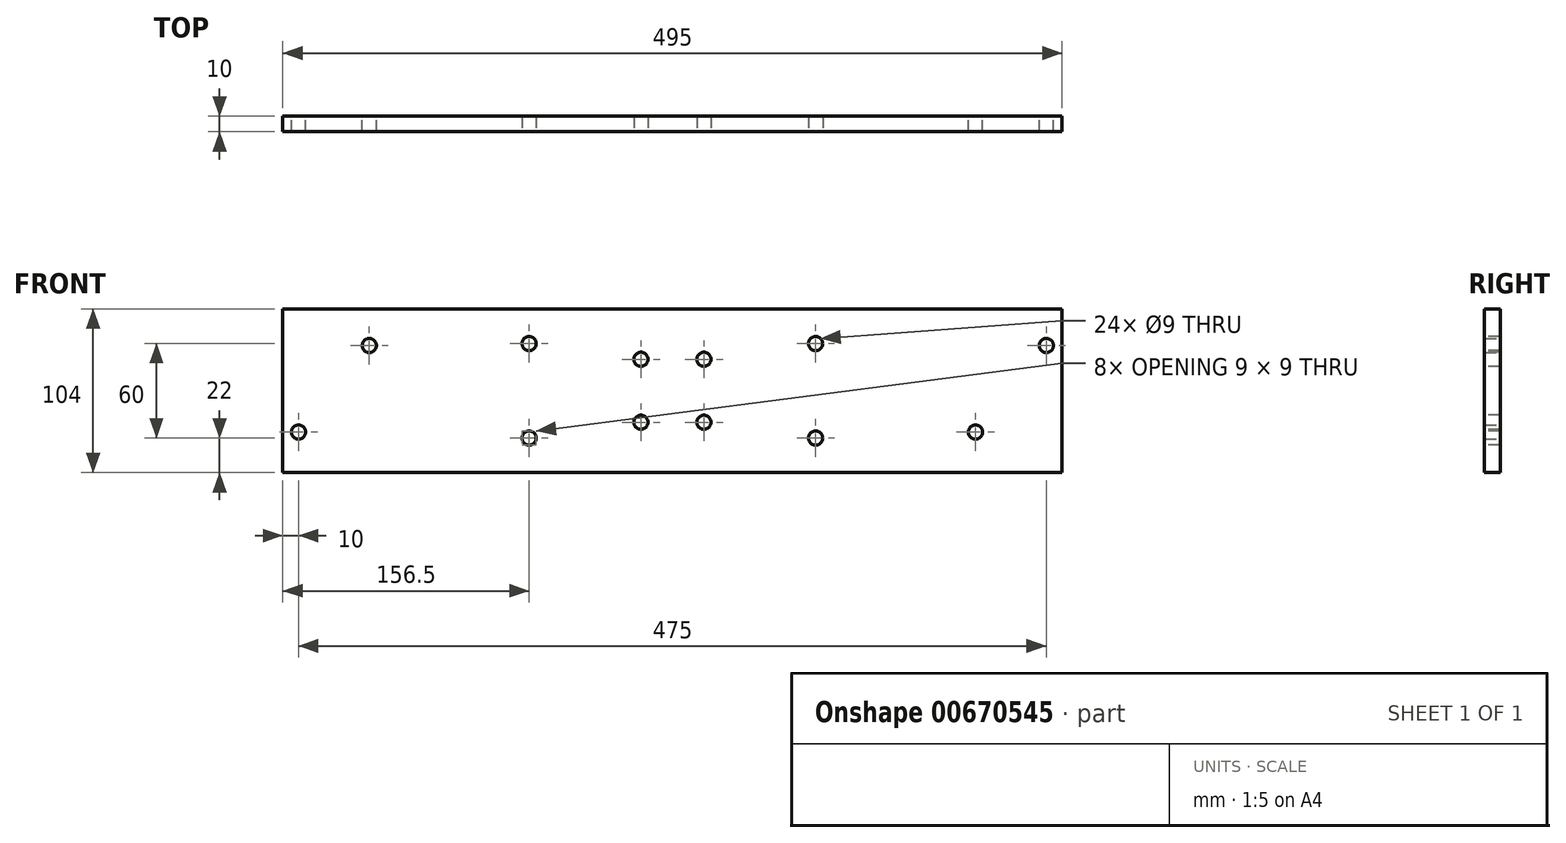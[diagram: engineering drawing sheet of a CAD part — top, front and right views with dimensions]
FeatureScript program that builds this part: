
annotation { "Feature Type Name" : "Feature", "Feature Type Description" : "" }
export const myFeature = defineFeature(function(context is Context, id is Id, definition is map)
    precondition{}
    {
        {
            var Q0;
            Q0=qCreatedBy(makeId("Right.planeOp"),FACE);
            var sketch = newSketch(context, id + "F0", { "sketchPlane" : qUnion([Q0])});
            skLineSegment(sketch, "E0.bottom", {"start": v(-5, 52) * mm, "end": v(5, 52) * mm});
            skLineSegment(sketch, "E0.top", {"start": v(-5, -52) * mm, "end": v(5, -52) * mm});
            skLineSegment(sketch, "E0.left", {"start": v(-5, 52) * mm, "end": v(-5, -52) * mm});
            skLineSegment(sketch, "E0.right", {"start": v(5, 52) * mm, "end": v(5, -52) * mm});
            skSolve(sketch);
        }
        {
            var Q0;
            Q0=makeQuery(id+"F0.imprint","IMPRINT",FACE,{"disambiguationData":[TD([[makeQuery(id+"F0.imprint","IMPRINT",EDGE,{"derivedFrom":sQuery(id+"F0.wireOp",EDGE,"E0.bottom")}),-1.0]])]});
            extrude(context, id + "F1", {"entities" : qUnion([Q0]), "depth" : 495 * mm, "offsetDistance" : 25 * mm, "symmetric" : true});
        }
        {
            var Q0;
            Q0=makeQuery(id+"F1.opExtrude","SWEPT_FACE",FACE,{"disambiguationData":[OSD([sQuery(id+"F0.wireOp",EDGE,"E0.left")])]});
            var sketch = newSketch(context, id + "F2", { "sketchPlane" : qUnion([Q0])});
            skPoint(sketch, "E1", {"position": v(-192.5, 28.76) * mm});
            skPoint(sketch, "E2", {"position": v(-237.5, -26.24) * mm});
            skPoint(sketch, "E3", {"position": v(237.5, 28.76) * mm});
            skPoint(sketch, "E4", {"position": v(192.5, -26.24) * mm});
            skPoint(sketch, "E5", {"position": v(-64.62, 26.03) * mm});
            skPoint(sketch, "E6", {"position": v(-64.62, -21.93) * mm});
            skPoint(sketch, "E7", {"position": v(44.92, 26.03) * mm});
            skPoint(sketch, "E8", {"position": v(44.92, -21.93) * mm});
            skPoint(sketch, "E9", {"position": v(215, 0) * mm});
            skPoint(sketch, "E10", {"position": v(-215, 0) * mm});
            skSolve(sketch);
        }
        {
            var Q0;
            Q0=sQuery(id+"F2.wireOp",VERTEX,"E1");
            var Q1;
            Q1=sQuery(id+"F2.wireOp",VERTEX,"E2");
            var Q2;
            Q2=sQuery(id+"F2.wireOp",VERTEX,"E3");
            var Q3;
            Q3=sQuery(id+"F2.wireOp",VERTEX,"E4");
            var Q4;
            Q4=makeQuery(id+"F1.opExtrude","SWEPT_BODY",BODY,{"disambiguationData":[OSD([sQuery(id+"F0.wireOp",EDGE,"E0.bottom"),sQuery(id+"F0.wireOp",EDGE,"E0.top"),sQuery(id+"F0.wireOp",EDGE,"E0.left"),sQuery(id+"F0.wireOp",EDGE,"E0.right")])]});
            hole(context, id + "F3", {"style" : HoleStyle.SIMPLE, "endStyle" : HoleEndStyle.BLIND, "standardTappedOrClearance" : lookupTablePath({ "fit" : "Normal", "standard" : "ISO", "size" : "M8", "type" : "Clearance" }), "standardBlindInLast" : lookupTablePath({ "fit" : "Normal", "standard" : "ISO", "size" : "M8", "type" : "Clearance" }), "holeDiameter" : 9 * mm, "majorDiameter" : 5 * mm, "holeDepth" : 18 * mm, "isTappedThrough" : true, "tappedDepth" : 15 * mm, "tapClearance" : 3, "locations" : qUnion([Q0, Q1, Q2, Q3]), "scope" : qUnion([Q4]), "startStyle" : HoleStartStyle.PART});
        }
        {
            var Q0;
            Q0=makeQuery(id+"F1.opExtrude","SWEPT_FACE",FACE,{"disambiguationData":[OSD([sQuery(id+"F0.wireOp",EDGE,"E0.right")])]});
            var sketch = newSketch(context, id + "F4", { "sketchPlane" : qUnion([Q0])});
            skPoint(sketch, "E11", {"position": v(-20, -20) * mm});
            skPoint(sketch, "E12", {"position": v(20, -20) * mm});
            skPoint(sketch, "E13", {"position": v(-20, 20) * mm});
            skPoint(sketch, "E14", {"position": v(20, 20) * mm});
            skPoint(sketch, "E15", {"position": v(91, 30) * mm});
            skPoint(sketch, "E16", {"position": v(91, -30) * mm});
            skPoint(sketch, "E17", {"position": v(-91, 30) * mm});
            skPoint(sketch, "E18", {"position": v(-91, -30) * mm});
            skSolve(sketch);
        }
        {
            var Q0;
            Q0=sQuery(id+"F4.wireOp",VERTEX,"E13");
            var Q1;
            Q1=sQuery(id+"F4.wireOp",VERTEX,"E14");
            var Q2;
            Q2=sQuery(id+"F4.wireOp",VERTEX,"E11");
            var Q3;
            Q3=sQuery(id+"F4.wireOp",VERTEX,"E12");
            var Q4;
            Q4=sQuery(id+"F4.wireOp",VERTEX,"E15");
            var Q5;
            Q5=sQuery(id+"F4.wireOp",VERTEX,"E16");
            var Q6;
            Q6=sQuery(id+"F4.wireOp",VERTEX,"E18");
            var Q7;
            Q7=sQuery(id+"F4.wireOp",VERTEX,"E17");
            var Q8;
            Q8=makeQuery(id+"F1.opExtrude","SWEPT_BODY",BODY,{"disambiguationData":[OSD([sQuery(id+"F0.wireOp",EDGE,"E0.bottom"),sQuery(id+"F0.wireOp",EDGE,"E0.top"),sQuery(id+"F0.wireOp",EDGE,"E0.left"),sQuery(id+"F0.wireOp",EDGE,"E0.right")])]});
            hole(context, id + "F5", {"style" : HoleStyle.SIMPLE, "endStyle" : HoleEndStyle.BLIND, "standardTappedOrClearance" : lookupTablePath({ "fit" : "Normal", "standard" : "ISO", "size" : "M8", "type" : "Clearance" }), "standardBlindInLast" : lookupTablePath({ "fit" : "Normal", "standard" : "ISO", "size" : "M8", "type" : "Clearance" }), "holeDiameter" : 9 * mm, "majorDiameter" : 8 * mm, "holeDepth" : 18 * mm, "isTappedThrough" : true, "tappedDepth" : 15 * mm, "tapClearance" : 3, "locations" : qUnion([Q0, Q1, Q2, Q3, Q4, Q5, Q6, Q7]), "scope" : qUnion([Q8]), "startStyle" : HoleStartStyle.PART});
        }
    });
